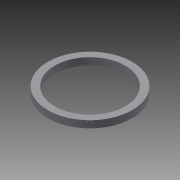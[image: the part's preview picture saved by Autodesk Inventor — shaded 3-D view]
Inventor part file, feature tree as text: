
AUTODESK INVENTOR PART (.ipt)
format: ipt  version: 2013 (Build 170138000, 138)  size: 74,240 bytes
history: native  units: mm
features: extrude x1, sketch x1
ambient origin geometry x8: Origin, YZ Plane, XZ Plane, XY Plane, X Axis, Y Axis, Z Axis, Center Point
bodies: Solid1 (feature_tree)
feature tree (2):
  extrude  "Extrusion1"  Depth=18.0mm
  sketch  "Sketch1"  dims[d0=15.1mm d2=18.0mm d3=1.5mm d4=0.0mm]
